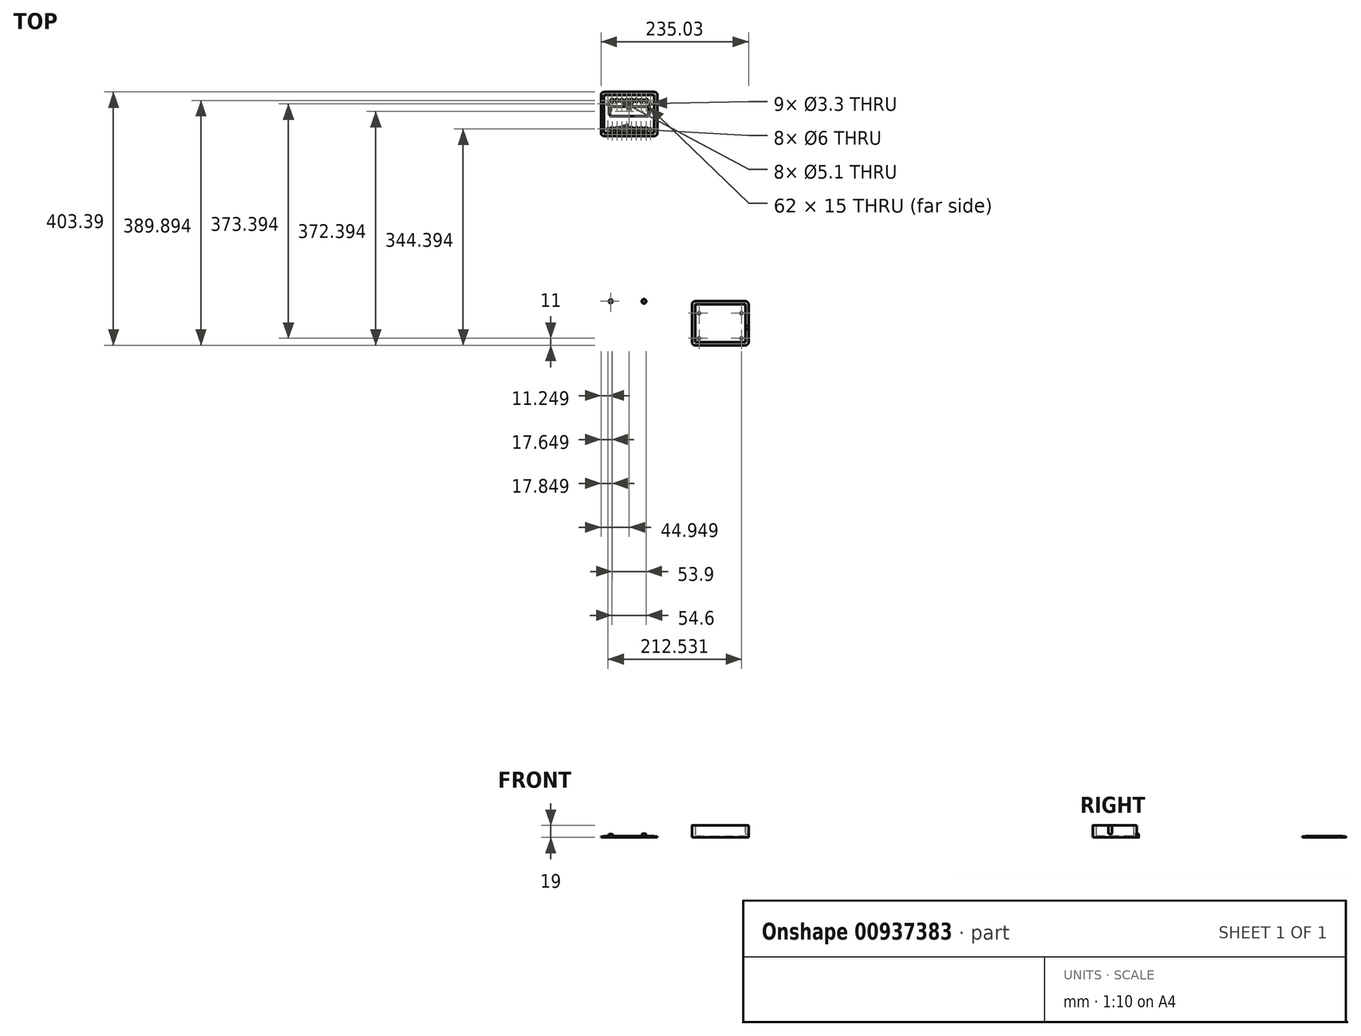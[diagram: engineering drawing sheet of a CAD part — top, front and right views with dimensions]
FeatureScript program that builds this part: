
annotation { "Feature Type Name" : "Feature", "Feature Type Description" : "" }
export const myFeature = defineFeature(function(context is Context, id is Id, definition is map)
    precondition{}
    {
        {
            var Q0;
            Q0=qCreatedBy(makeId("Top.planeOp"),FACE);
            var sketch = newSketch(context, id + "F0", { "sketchPlane" : qUnion([Q0])});
            skLineSegment(sketch, "E0.bottom", {"start": v(5, 0) * mm, "end": v(85, 0) * mm});
            skLineSegment(sketch, "E0.top", {"start": v(5, -70) * mm, "end": v(85, -70) * mm});
            skLineSegment(sketch, "E0.left", {"start": v(0, -5) * mm, "end": v(0, -65) * mm});
            skLineSegment(sketch, "E0.right", {"start": v(90, -5) * mm, "end": v(90, -65) * mm});
            skLineSegment(sketch, "E1.0", {"start": v(5, -5) * mm, "end": v(5, -65) * mm});
            skLineSegment(sketch, "E1.1", {"start": v(5, -5) * mm, "end": v(85, -5) * mm});
            skLineSegment(sketch, "E1.2", {"start": v(85, -5) * mm, "end": v(85, -65) * mm});
            skLineSegment(sketch, "E1.3", {"start": v(5, -65) * mm, "end": v(85, -65) * mm});
            skPoint(sketch, "E2.visualSharp", {"position": v(0, 0) * mm});
            skArc(sketch, "E2.filletArc", {"start": v(5, 0) * mm, "mid": v(1.46, -1.46) * mm, "end": v(0, -5) * mm});
            skPoint(sketch, "E3.visualSharp", {"position": v(90, 0) * mm});
            skArc(sketch, "E3.filletArc", {"start": v(90, -5) * mm, "mid": v(88.54, -1.46) * mm, "end": v(85, 0) * mm});
            skPoint(sketch, "E4.visualSharp", {"position": v(90, -70) * mm});
            skArc(sketch, "E4.filletArc", {"start": v(85, -70) * mm, "mid": v(88.54, -68.54) * mm, "end": v(90, -65) * mm});
            skPoint(sketch, "E5.visualSharp", {"position": v(0, -70) * mm});
            skArc(sketch, "E5.filletArc", {"start": v(0, -65) * mm, "mid": v(1.46, -68.54) * mm, "end": v(5, -70) * mm});
            skCircle(sketch, "E6", {"center": v(11.25, -59) * mm, "radius": 1.65 * mm});
            skLineSegment(sketch, "E7", {"start": v(45, -65) * mm, "end": v(45, -53.02) * mm, "construction": true});
            skCircle(sketch, "E8.MirrorC", {"center": v(78.75, -59) * mm, "radius": 1.65 * mm});
            skLineSegment(sketch, "E9", {"start": v(8.68, -39) * mm, "end": v(18.91, -39) * mm, "construction": true});
            skCircle(sketch, "E10.MirrorC", {"center": v(11.25, -19) * mm, "radius": 1.65 * mm});
            skCircle(sketch, "E11.MirrorC", {"center": v(78.75, -19) * mm, "radius": 1.65 * mm});
            skSolve(sketch);
        }
        {
            var Q0;
            Q0=makeQuery(id+"F0.imprint","IMPRINT",FACE,{"disambiguationData":[TD([[makeQuery(id+"F0.imprint","IMPRINT",EDGE,{"derivedFrom":sQuery(id+"F0.wireOp",EDGE,"E1.0")}),1.0]])]});
            extrude(context, id + "F1", {"entities" : qUnion([Q0]), "depth" : 2 * mm, "offsetDistance" : 25 * mm});
        }
        {
            var Q0;
            Q0=makeQuery(id+"F0.imprint","IMPRINT",FACE,{"disambiguationData":[TD([[makeQuery(id+"F0.imprint","IMPRINT",EDGE,{"derivedFrom":sQuery(id+"F0.wireOp",EDGE,"E0.bottom")}),-1.0]])]});
            extrude(context, id + "F2", {"entities" : qUnion([Q0]), "operationType" : NewBodyOperationType.ADD, "depth" : 19 * mm, "offsetDistance" : 25 * mm});
        }
        {
            var Q0;
            Q0=makeQuery(id+"F2.opExtrude","SWEPT_FACE",FACE,{"disambiguationData":[OSD([sQuery(id+"F0.wireOp",EDGE,"E0.right")])]});
            var sketch = newSketch(context, id + "F3", { "sketchPlane" : qUnion([Q0])});
            skPoint(sketch, "E12", {"position": v(-42, 11.5) * mm});
            skArc(sketch, "E13", {"start": v(-45, 8) * mm, "mid": v(-42, 5) * mm, "end": v(-39, 8) * mm});
            skLineSegment(sketch, "E14", {"start": v(-45, 8) * mm, "end": v(-45, 19) * mm});
            skLineSegment(sketch, "E15", {"start": v(-39, 8) * mm, "end": v(-39, 19) * mm});
            skSolve(sketch);
        }
        {
            var Q0;
            Q0=makeQuery(id+"F3.imprint","IMPRINT",FACE,{"disambiguationData":[TD([[makeQuery(id+"F3.imprint","IMPRINT",EDGE,{"derivedFrom":sQuery(id+"F3.wireOp",EDGE,"E13")}),1.0]])]});
            extrude(context, id + "F4", {"entities" : qUnion([Q0]), "operationType" : NewBodyOperationType.REMOVE, "oppositeDirection" : true, "depth" : 25 * mm, "offsetDistance" : 25 * mm});
        }
        {
            var Q0;
            Q0=qCreatedBy(makeId("Top.planeOp"),FACE);
            var sketch = newSketch(context, id + "F5", { "sketchPlane" : qUnion([Q0])});
            skLineSegment(sketch, "E16.bottom", {"start": v(-140.03, 333.4) * mm, "end": v(-60.03, 333.4) * mm});
            skLineSegment(sketch, "E16.top", {"start": v(-140.03, 263.4) * mm, "end": v(-60.03, 263.4) * mm});
            skLineSegment(sketch, "E16.left", {"start": v(-145.03, 328.4) * mm, "end": v(-145.03, 268.4) * mm});
            skLineSegment(sketch, "E16.right", {"start": v(-55.03, 328.4) * mm, "end": v(-55.03, 268.4) * mm});
            skLineSegment(sketch, "E17.0", {"start": v(-140.03, 328.4) * mm, "end": v(-140.03, 268.4) * mm});
            skLineSegment(sketch, "E17.1", {"start": v(-140.03, 328.4) * mm, "end": v(-60.03, 328.4) * mm});
            skLineSegment(sketch, "E17.2", {"start": v(-60.03, 328.4) * mm, "end": v(-60.03, 268.4) * mm});
            skLineSegment(sketch, "E17.3", {"start": v(-140.03, 268.4) * mm, "end": v(-60.03, 268.4) * mm});
            skPoint(sketch, "E18.visualSharp", {"position": v(-145.03, 333.4) * mm});
            skArc(sketch, "E18.filletArc", {"start": v(-140.03, 333.4) * mm, "mid": v(-143.57, 331.93) * mm, "end": v(-145.03, 328.4) * mm});
            skArc(sketch, "E19.filletArc", {"start": v(-55.03, 328.4) * mm, "mid": v(-56.5, 331.93) * mm, "end": v(-60.03, 333.4) * mm});
            skPoint(sketch, "E20.visualSharp", {"position": v(-55.03, 263.4) * mm});
            skArc(sketch, "E20.filletArc", {"start": v(-60.03, 263.4) * mm, "mid": v(-56.5, 264.86) * mm, "end": v(-55.03, 268.4) * mm});
            skPoint(sketch, "E21.visualSharp", {"position": v(-145.03, 263.4) * mm});
            skArc(sketch, "E21.filletArc", {"start": v(-145.03, 268.4) * mm, "mid": v(-143.57, 264.86) * mm, "end": v(-140.03, 263.4) * mm});
            skCircle(sketch, "E22", {"center": v(-133.78, 274.4) * mm, "radius": 1.65 * mm});
            skLineSegment(sketch, "E23", {"start": v(-100.03, 268.4) * mm, "end": v(-100.03, 280.38) * mm, "construction": true});
            skCircle(sketch, "E24.MirrorC", {"center": v(-66.28, 274.4) * mm, "radius": 1.65 * mm});
            skLineSegment(sketch, "E25", {"start": v(-136.35, 294.4) * mm, "end": v(-126.12, 294.4) * mm, "construction": true});
            skCircle(sketch, "E26.MirrorC", {"center": v(-133.78, 314.4) * mm, "radius": 1.65 * mm});
            skCircle(sketch, "E27.MirrorC", {"center": v(-66.28, 314.4) * mm, "radius": 1.65 * mm});
            skLineSegment(sketch, "E28.bottom", {"start": v(-69.08, 294.9) * mm, "end": v(-131.08, 294.9) * mm});
            skLineSegment(sketch, "E28.top", {"start": v(-69.08, 309.9) * mm, "end": v(-131.08, 309.9) * mm});
            skLineSegment(sketch, "E28.left", {"start": v(-69.08, 294.9) * mm, "end": v(-69.08, 309.9) * mm});
            skLineSegment(sketch, "E28.right", {"start": v(-131.08, 294.9) * mm, "end": v(-131.08, 309.9) * mm});
            skPoint(sketch, "E28.middle", {"position": v(-100.08, 302.4) * mm});
            skCircle(sketch, "E29", {"center": v(-72.78, 319.9) * mm, "radius": 2.55 * mm});
            skCircle(sketch, "E30.1.0.0", {"center": v(-80.58, 319.9) * mm, "radius": 2.55 * mm});
            skCircle(sketch, "E30.2.0.0", {"center": v(-88.38, 319.9) * mm, "radius": 2.55 * mm});
            skCircle(sketch, "E30.3.0.0", {"center": v(-96.18, 319.9) * mm, "radius": 2.55 * mm});
            skCircle(sketch, "E30.4.0.0", {"center": v(-103.98, 319.9) * mm, "radius": 2.55 * mm});
            skCircle(sketch, "E30.5.0.0", {"center": v(-111.78, 319.9) * mm, "radius": 2.55 * mm});
            skCircle(sketch, "E30.6.0.0", {"center": v(-119.58, 319.9) * mm, "radius": 2.55 * mm});
            skCircle(sketch, "E30.7.0.0", {"center": v(-127.38, 319.9) * mm, "radius": 2.55 * mm});
            skLineSegment(sketch, "E30.direction1", {"start": v(-72.78, 319.9) * mm, "end": v(-80.58, 319.9) * mm, "construction": true});
            skCircle(sketch, "E31", {"center": v(-73.28, 274.4) * mm, "radius": 3 * mm});
            skCircle(sketch, "E32.1.0.0", {"center": v(-80.98, 274.4) * mm, "radius": 3 * mm});
            skCircle(sketch, "E32.2.0.0", {"center": v(-88.68, 274.4) * mm, "radius": 3 * mm});
            skCircle(sketch, "E32.3.0.0", {"center": v(-96.38, 274.4) * mm, "radius": 3 * mm});
            skCircle(sketch, "E32.4.0.0", {"center": v(-104.08, 274.4) * mm, "radius": 3 * mm});
            skCircle(sketch, "E32.5.0.0", {"center": v(-111.78, 274.4) * mm, "radius": 3 * mm});
            skCircle(sketch, "E32.6.0.0", {"center": v(-119.48, 274.4) * mm, "radius": 3 * mm});
            skCircle(sketch, "E32.7.0.0", {"center": v(-127.18, 274.4) * mm, "radius": 3 * mm});
            skLineSegment(sketch, "E32.direction1", {"start": v(-73.28, 274.4) * mm, "end": v(-80.98, 274.4) * mm, "construction": true});
            skSolve(sketch);
        }
        {
            var Q0;
            Q0=makeQuery(id+"F5.imprint","IMPRINT",FACE,{"disambiguationData":[TD([[makeQuery(id+"F5.imprint","IMPRINT",EDGE,{"derivedFrom":sQuery(id+"F5.wireOp",EDGE,"E17.0")}),1.0]])]});
            extrude(context, id + "F6", {"entities" : qUnion([Q0]), "depth" : 2.4 * mm, "offsetDistance" : 25 * mm});
        }
        {
            var Q0;
            Q0=makeQuery(id+"F5.imprint","IMPRINT",FACE,{"disambiguationData":[TD([[makeQuery(id+"F5.imprint","IMPRINT",EDGE,{"derivedFrom":sQuery(id+"F5.wireOp",EDGE,"E16.bottom")}),-1.0]])]});
            extrude(context, id + "F7", {"entities" : qUnion([Q0]), "operationType" : NewBodyOperationType.ADD, "depth" : 1.2 * mm, "offsetDistance" : 25 * mm});
        }
        {
            var Q0;
            Q0=qCreatedBy(makeId("Top.planeOp"),FACE);
            var sketch = newSketch(context, id + "F8", { "sketchPlane" : qUnion([Q0])});
            skCircle(sketch, "E33", {"center": v(-76.58, 0) * mm, "radius": 3.5 * mm});
            skSolve(sketch);
        }
        {
            var Q0;
            Q0=makeQuery(id+"F8.imprint","IMPRINT",FACE,{"disambiguationData":[TD([[makeQuery(id+"F8.imprint","IMPRINT",EDGE,{"derivedFrom":sQuery(id+"F8.wireOp",EDGE,"E33")}),1.0]])]});
            extrude(context, id + "F9", {"entities" : qUnion([Q0]), "depth" : 1 * mm, "offsetDistance" : 25 * mm});
        }
        {
            var Q0;
            Q0=makeQuery(id+"F9.opExtrude","CAP_FACE",FACE,{"disambiguationData":[OSD([sQuery(id+"F8.wireOp",EDGE,"E33")])],"isStart":false});
            var sketch = newSketch(context, id + "F10", { "sketchPlane" : qUnion([Q0])});
            skCircle(sketch, "E34", {"center": v(-76.58, 0) * mm, "radius": 2.8 * mm});
            skSolve(sketch);
        }
        {
            var Q0;
            Q0 = qSketchRegion(id + "F10", true);
            extrude(context, id + "F11", {"entities" : qUnion([Q0]), "operationType" : NewBodyOperationType.ADD, "depth" : 5 * mm, "offsetDistance" : 25 * mm});
        }
        {
            var Q0;
            Q0=makeQuery(id+"F11.opExtrude","CAP_EDGE",EDGE,{"disambiguationData":[OSD([sQuery(id+"F10.wireOp",EDGE,"E34")])],"isStart":false});
            fillet(context, id + "F12", {"entities" : qUnion([Q0]), "radius" : 0.4 * mm, "tangentPropagation" : true, "allowEdgeOverflow" : false});
        }
        {
            var Q0;
            Q0=qCreatedBy(makeId("Top.planeOp"),FACE);
            var sketch = newSketch(context, id + "F13", { "sketchPlane" : qUnion([Q0])});
            skCircle(sketch, "E35", {"center": v(-129.48, 0) * mm, "radius": 3 * mm});
            skCircle(sketch, "E36", {"center": v(-129.48, 0) * mm, "radius": 1.65 * mm});
            skSolve(sketch);
        }
        {
            var Q0;
            Q0=makeQuery(id+"F13.imprint","IMPRINT",FACE,{"disambiguationData":[TD([[makeQuery(id+"F13.imprint","IMPRINT",EDGE,{"derivedFrom":sQuery(id+"F13.wireOp",EDGE,"E35")}),1.0]])]});
            extrude(context, id + "F14", {"entities" : qUnion([Q0]), "depth" : 5 * mm, "offsetDistance" : 25 * mm});
        }
    });
